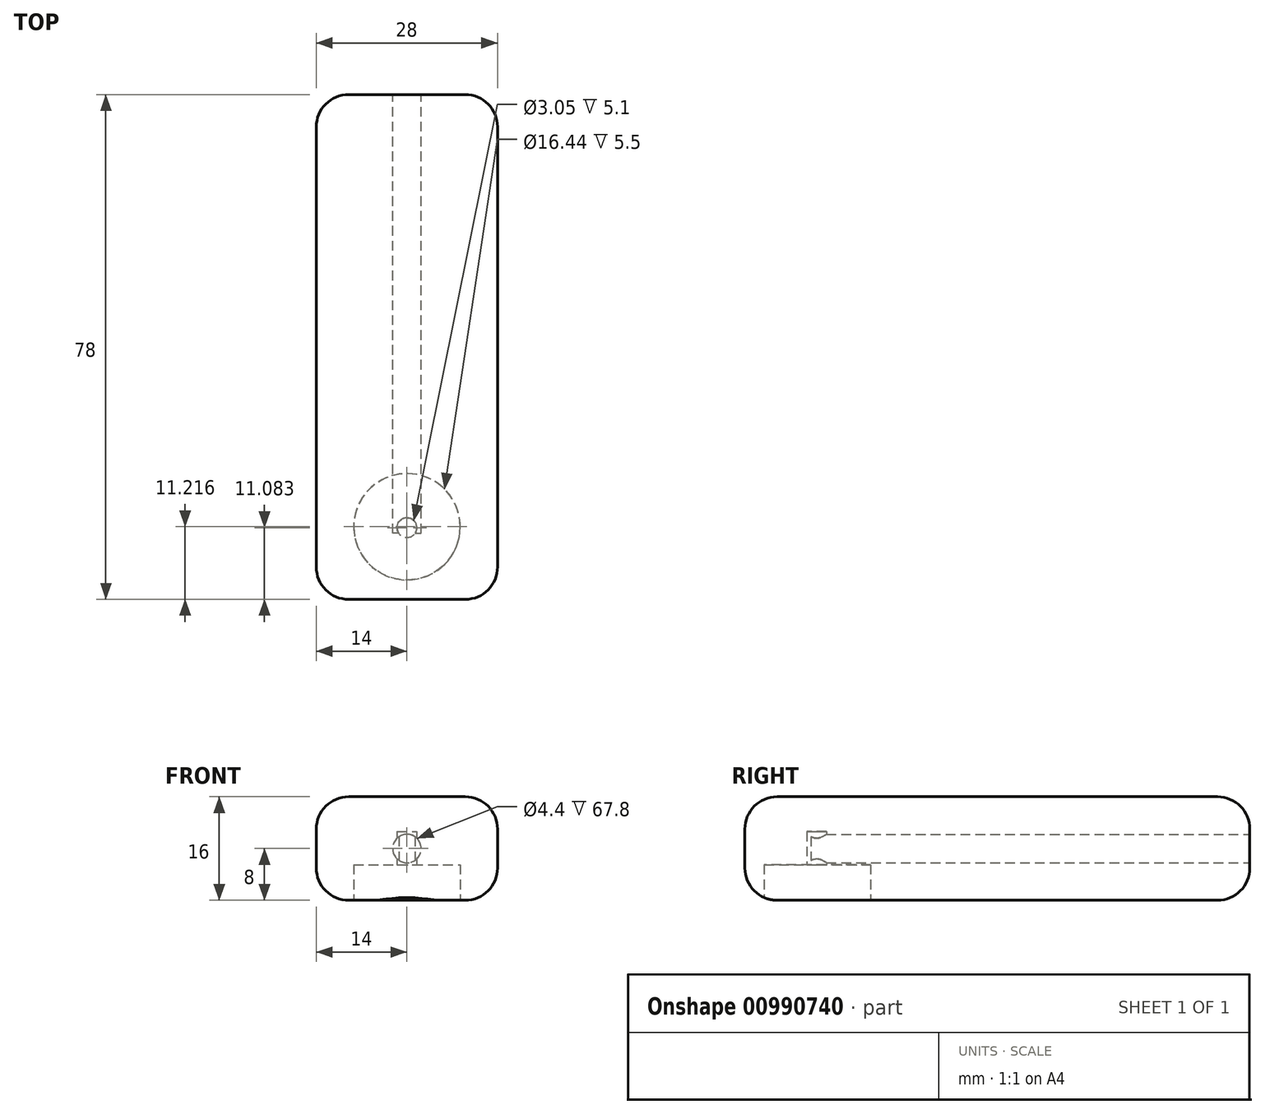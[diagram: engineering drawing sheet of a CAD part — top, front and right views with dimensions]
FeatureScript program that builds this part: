
annotation { "Feature Type Name" : "Feature", "Feature Type Description" : "" }
export const myFeature = defineFeature(function(context is Context, id is Id, definition is map)
    precondition{}
    {
        {
            var Q0;
            Q0=qCreatedBy(makeId("Front.planeOp"),FACE);
            var sketch = newSketch(context, id + "F0", { "sketchPlane" : qUnion([Q0])});
            skLineSegment(sketch, "E0.bottom", {"start": v(-14, 8) * mm, "end": v(14, 8) * mm});
            skLineSegment(sketch, "E0.top", {"start": v(-14, -8) * mm, "end": v(14, -8) * mm});
            skLineSegment(sketch, "E0.left", {"start": v(-14, 8) * mm, "end": v(-14, -8) * mm});
            skLineSegment(sketch, "E0.right", {"start": v(14, 8) * mm, "end": v(14, -8) * mm});
            skPoint(sketch, "E0.middle", {"position": v(0, 0) * mm});
            skSolve(sketch);
        }
        {
            var Q0;
            Q0=makeQuery(id+"F0.imprint","IMPRINT",FACE,{"disambiguationData":[TD([[makeQuery(id+"F0.imprint","IMPRINT",EDGE,{"derivedFrom":sQuery(id+"F0.wireOp",EDGE,"E0.bottom")}),-1.0]])]});
            extrude(context, id + "F1", {"entities" : qUnion([Q0]), "depth" : 78 * mm, "offsetDistance" : 25 * mm});
        }
        {
            var Q0;
            Q0=makeQuery(id+"F1.opExtrude","CAP_FACE",FACE,{"disambiguationData":[OSD([sQuery(id+"F0.wireOp",EDGE,"E0.bottom"),sQuery(id+"F0.wireOp",EDGE,"E0.top"),sQuery(id+"F0.wireOp",EDGE,"E0.left"),sQuery(id+"F0.wireOp",EDGE,"E0.right")])],"isStart":true});
            var sketch = newSketch(context, id + "F2", { "sketchPlane" : qUnion([Q0])});
            skCircle(sketch, "E1", {"center": v(0, 0) * mm, "radius": 2.2 * mm});
            skSolve(sketch);
        }
        {
            var Q0;
            Q0=makeQuery(id+"F1.opExtrude","SWEPT_FACE",FACE,{"disambiguationData":[OSD([sQuery(id+"F0.wireOp",EDGE,"E0.top")])]});
            var sketch = newSketch(context, id + "F3", { "sketchPlane" : qUnion([Q0])});
            skCircle(sketch, "E2", {"center": v(0, 66.78) * mm, "radius": 8.22 * mm});
            skPoint(sketch, "E2.centerSnap0", {"position": v(0, 78) * mm});
            skSolve(sketch);
        }
        {
            var Q0;
            Q0=makeQuery(id+"F2.imprint","IMPRINT",FACE,{"disambiguationData":[TD([[makeQuery(id+"F2.imprint","IMPRINT",EDGE,{"derivedFrom":sQuery(id+"F2.wireOp",EDGE,"E1")}),1.0]])]});
            extrude(context, id + "F4", {"entities" : qUnion([Q0]), "operationType" : NewBodyOperationType.REMOVE, "oppositeDirection" : true, "depth" : 67.8 * mm, "offsetDistance" : 25 * mm});
        }
        {
            var Q0;
            Q0=makeQuery(id+"F3.imprint","IMPRINT",FACE,{"disambiguationData":[TD([[makeQuery(id+"F3.imprint","IMPRINT",EDGE,{"derivedFrom":sQuery(id+"F3.wireOp",EDGE,"E2")}),1.0]])]});
            var sketch = newSketch(context, id + "F5", { "sketchPlane" : qUnion([Q0])});
            skCircle(sketch, "E3", {"center": v(0, 66.92) * mm, "radius": 1.53 * mm});
            skSolve(sketch);
        }
        {
            var Q0;
            Q0=makeQuery(id+"F5.imprint","IMPRINT",FACE,{"disambiguationData":[TD([[makeQuery(id+"F5.imprint","IMPRINT",EDGE,{"derivedFrom":sQuery(id+"F5.wireOp",EDGE,"E3")}),1.0]])]});
            extrude(context, id + "F6", {"entities" : qUnion([Q0]), "operationType" : NewBodyOperationType.REMOVE, "oppositeDirection" : true, "depth" : 10.6 * mm, "offsetDistance" : 25 * mm});
        }
        {
            var Q0;
            Q0=makeQuery(id+"F3.imprint","IMPRINT",FACE,{"disambiguationData":[TD([[makeQuery(id+"F3.imprint","IMPRINT",EDGE,{"derivedFrom":sQuery(id+"F3.wireOp",EDGE,"E2")}),1.0]])]});
            extrude(context, id + "F7", {"entities" : qUnion([Q0]), "operationType" : NewBodyOperationType.REMOVE, "oppositeDirection" : true, "depth" : 5.5 * mm, "offsetDistance" : 25 * mm});
        }
        {
            var Q0;
            Q0=makeQuery(id+"F1.opExtrude","SWEPT_EDGE",EDGE,{"disambiguationData":[OSD([sQuery(id+"F0.wireOp",EDGE,"E0.top"),sQuery(id+"F0.wireOp",EDGE,"E0.left")])]});
            var Q1;
            Q1=makeQuery(id+"F1.opExtrude","CAP_EDGE",EDGE,{"disambiguationData":[OSD([sQuery(id+"F0.wireOp",EDGE,"E0.top")])],"isStart":false});
            var Q2;
            Q2=makeQuery(id+"F1.opExtrude","SWEPT_EDGE",EDGE,{"disambiguationData":[OSD([sQuery(id+"F0.wireOp",EDGE,"E0.top"),sQuery(id+"F0.wireOp",EDGE,"E0.right")])]});
            var Q3;
            Q3=makeQuery(id+"F1.opExtrude","CAP_EDGE",EDGE,{"disambiguationData":[OSD([sQuery(id+"F0.wireOp",EDGE,"E0.top")])],"isStart":true});
            var Q4;
            Q4=makeQuery(id+"F1.opExtrude","CAP_EDGE",EDGE,{"disambiguationData":[OSD([sQuery(id+"F0.wireOp",EDGE,"E0.bottom")])],"isStart":true});
            var Q5;
            Q5=makeQuery(id+"F1.opExtrude","SWEPT_EDGE",EDGE,{"disambiguationData":[OSD([sQuery(id+"F0.wireOp",EDGE,"E0.bottom"),sQuery(id+"F0.wireOp",EDGE,"E0.right")])]});
            var Q6;
            Q6=makeQuery(id+"F1.opExtrude","CAP_EDGE",EDGE,{"disambiguationData":[OSD([sQuery(id+"F0.wireOp",EDGE,"E0.bottom")])],"isStart":false});
            var Q7;
            Q7=makeQuery(id+"F1.opExtrude","SWEPT_EDGE",EDGE,{"disambiguationData":[OSD([sQuery(id+"F0.wireOp",EDGE,"E0.bottom"),sQuery(id+"F0.wireOp",EDGE,"E0.left")])]});
            var Q8;
            Q8=makeQuery(id+"F1.opExtrude","CAP_EDGE",EDGE,{"disambiguationData":[OSD([sQuery(id+"F0.wireOp",EDGE,"E0.right")])],"isStart":false});
            var Q9;
            Q9=makeQuery(id+"F1.opExtrude","CAP_EDGE",EDGE,{"disambiguationData":[OSD([sQuery(id+"F0.wireOp",EDGE,"E0.left")])],"isStart":false});
            var Q10;
            Q10=makeQuery(id+"F1.opExtrude","CAP_EDGE",EDGE,{"disambiguationData":[OSD([sQuery(id+"F0.wireOp",EDGE,"E0.left")])],"isStart":true});
            var Q11;
            Q11=makeQuery(id+"F1.opExtrude","CAP_EDGE",EDGE,{"disambiguationData":[OSD([sQuery(id+"F0.wireOp",EDGE,"E0.right")])],"isStart":true});
            fillet(context, id + "F8", {"entities" : qUnion([Q0, Q1, Q2, Q3, Q4, Q5, Q6, Q7, Q8, Q9, Q10, Q11]), "radius" : 5 * mm, "tangentPropagation" : true, "allowEdgeOverflow" : false});
        }
    });
